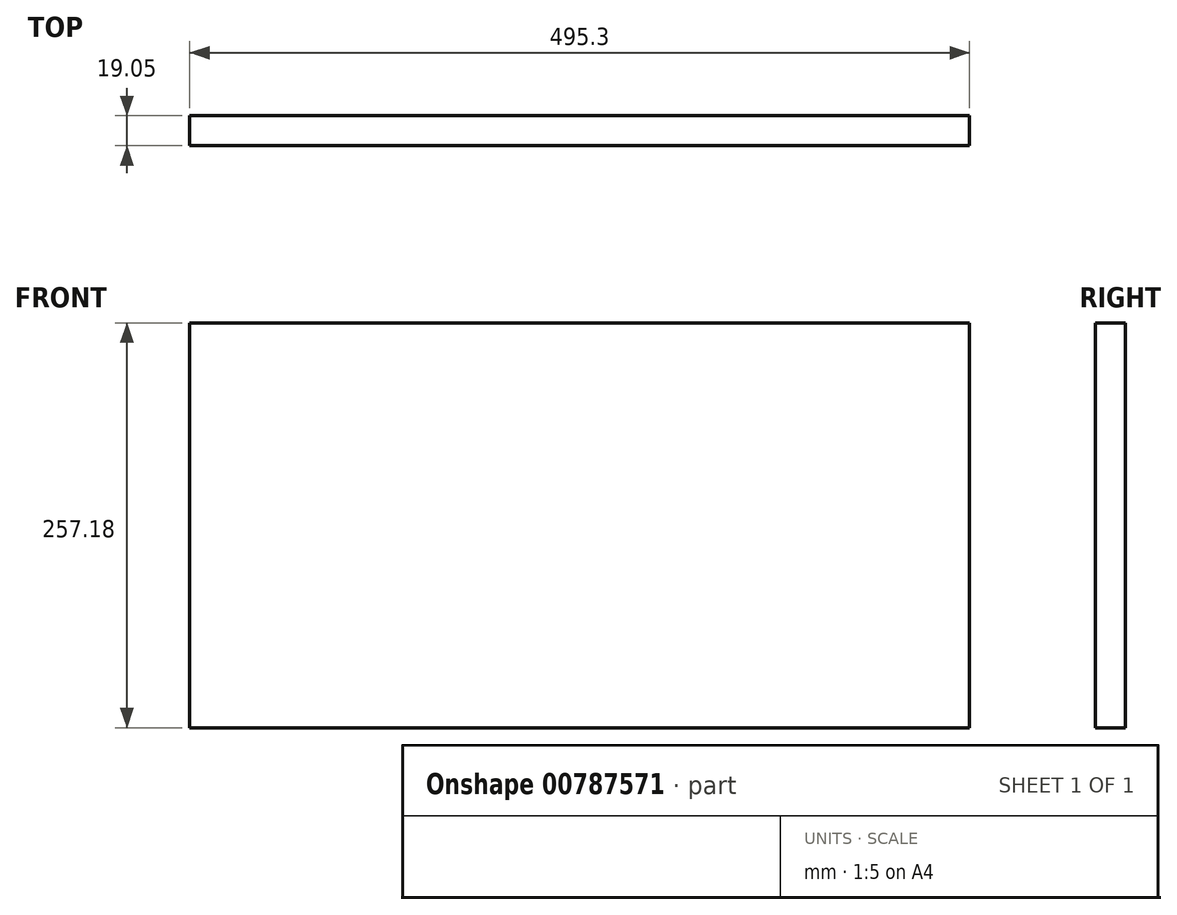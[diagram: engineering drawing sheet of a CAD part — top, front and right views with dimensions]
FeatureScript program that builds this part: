
annotation { "Feature Type Name" : "Feature", "Feature Type Description" : "" }
export const myFeature = defineFeature(function(context is Context, id is Id, definition is map)
    precondition{}
    {
        {
            var Q0;
            Q0=qCreatedBy(makeId("Front.planeOp"),FACE);
            var sketch = newSketch(context, id + "F0", { "sketchPlane" : qUnion([Q0])});
            skLineSegment(sketch, "E0.bottom", {"start": v(247.65, 128.59) * mm, "end": v(-247.65, 128.59) * mm});
            skLineSegment(sketch, "E0.top", {"start": v(247.65, -128.59) * mm, "end": v(-247.65, -128.59) * mm});
            skLineSegment(sketch, "E0.left", {"start": v(247.65, 128.59) * mm, "end": v(247.65, -128.59) * mm});
            skLineSegment(sketch, "E0.right", {"start": v(-247.65, 128.59) * mm, "end": v(-247.65, -128.59) * mm});
            skPoint(sketch, "E0.middle", {"position": v(0, 0) * mm});
            skSolve(sketch);
        }
        {
            var Q0;
            Q0=makeQuery(id+"F0.imprint","IMPRINT",FACE,{"disambiguationData":[TD([[makeQuery(id+"F0.imprint","IMPRINT",EDGE,{"derivedFrom":sQuery(id+"F0.wireOp",EDGE,"E0.bottom")}),1.0]])]});
            extrude(context, id + "F1", {"entities" : qUnion([Q0]), "depth" : 19.05 * mm, "offsetDistance" : 25.4 * mm});
        }
    });
